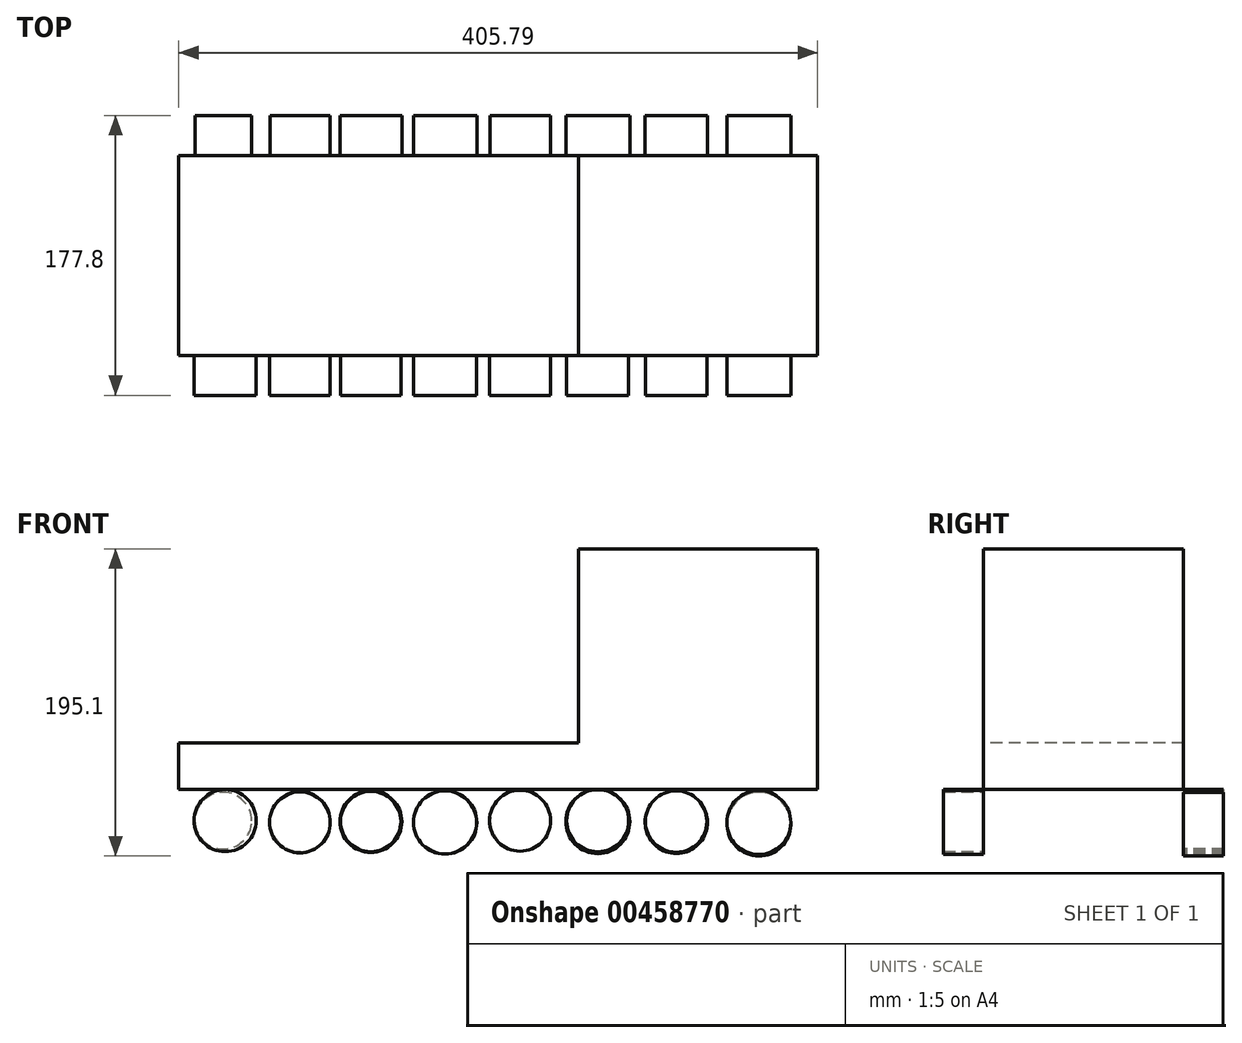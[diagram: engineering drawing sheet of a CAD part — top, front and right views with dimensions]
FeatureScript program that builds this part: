
annotation { "Feature Type Name" : "Feature", "Feature Type Description" : "" }
export const myFeature = defineFeature(function(context is Context, id is Id, definition is map)
    precondition{}
    {
        {
            var Q0;
            Q0=qCreatedBy(makeId("Front.planeOp"),FACE);
            var sketch = newSketch(context, id + "F0", { "sketchPlane" : qUnion([Q0])});
            skLineSegment(sketch, "E0.bottom", {"start": v(-76.2, 76.35) * mm, "end": v(75.6, 76.35) * mm});
            skLineSegment(sketch, "E0.top", {"start": v(-76.2, -76.35) * mm, "end": v(75.6, -76.35) * mm});
            skLineSegment(sketch, "E0.left", {"start": v(-76.2, 76.35) * mm, "end": v(-76.2, -76.35) * mm});
            skLineSegment(sketch, "E0.right", {"start": v(75.6, 76.35) * mm, "end": v(75.6, -76.35) * mm});
            skSolve(sketch);
        }
        {
            var Q0;
            Q0=makeQuery(id+"F0.imprint","IMPRINT",FACE,{"disambiguationData":[TD([[makeQuery(id+"F0.imprint","IMPRINT",EDGE,{"derivedFrom":sQuery(id+"F0.wireOp",EDGE,"E0.bottom")}),-1.0]])]});
            extrude(context, id + "F1", {"entities" : qUnion([Q0]), "depth" : 127 * mm});
        }
        {
            var Q0;
            Q0=makeQuery(id+"F1.opExtrude","SWEPT_FACE",FACE,{"disambiguationData":[OSD([sQuery(id+"F0.wireOp",EDGE,"E0.left")])]});
            var sketch = newSketch(context, id + "F2", { "sketchPlane" : qUnion([Q0])});
            skLineSegment(sketch, "E1.bottom", {"start": v(0, -46.8) * mm, "end": v(127, -46.8) * mm});
            skLineSegment(sketch, "E1.top", {"start": v(0, -76.35) * mm, "end": v(127, -76.35) * mm});
            skLineSegment(sketch, "E1.left", {"start": v(0, -46.8) * mm, "end": v(0, -76.35) * mm});
            skLineSegment(sketch, "E1.right", {"start": v(127, -46.8) * mm, "end": v(127, -76.35) * mm});
            skSolve(sketch);
        }
        {
            var Q0;
            Q0=makeQuery(id+"F2.imprint","IMPRINT",FACE,{"disambiguationData":[TD([[makeQuery(id+"F2.imprint","IMPRINT",EDGE,{"derivedFrom":sQuery(id+"F2.wireOp",EDGE,"E1.bottom")}),-1.0]])]});
            extrude(context, id + "F3", {"entities" : qUnion([Q0]), "operationType" : NewBodyOperationType.ADD, "depth" : 254 * mm});
        }
        {
            var Q0;
            Q0=makeQuery(id+"F3.boolean.opBoolean","MERGE",FACE,{"derivedFrom":[makeQuery(id+"F1.opExtrude","CAP_FACE",FACE,{"disambiguationData":[OSD([sQuery(id+"F0.wireOp",EDGE,"E0.bottom"),sQuery(id+"F0.wireOp",EDGE,"E0.top"),sQuery(id+"F0.wireOp",EDGE,"E0.left"),sQuery(id+"F0.wireOp",EDGE,"E0.right")])],"isStart":false}),makeQuery(id+"F3.opExtrude","SWEPT_FACE",FACE,{"disambiguationData":[OSD([sQuery(id+"F2.wireOp",EDGE,"E1.right")])]})]});
            var sketch = newSketch(context, id + "F4", { "sketchPlane" : qUnion([Q0])});
            skCircle(sketch, "E2", {"center": v(-300.7, -96.24) * mm, "radius": 19.7 * mm});
            skSolve(sketch);
        }
        {
            var Q0;
            Q0=makeQuery(id+"F4.imprint","IMPRINT",FACE,{"disambiguationData":[TD([[makeQuery(id+"F4.imprint","IMPRINT",EDGE,{"derivedFrom":makeQuery(id+"F1.opExtrude","CAP_EDGE",EDGE,{"disambiguationData":[OSD([sQuery(id+"F0.wireOp",EDGE,"E0.bottom")])],"isStart":false})}),-1.0]])]});
            var sketch = newSketch(context, id + "F5", { "sketchPlane" : qUnion([Q0])});
            skCircle(sketch, "E3", {"center": v(-253.23, -97.4) * mm, "radius": 19.32 * mm});
            skCircle(sketch, "E4", {"center": v(-208.22, -96.86) * mm, "radius": 19.15 * mm});
            skCircle(sketch, "E5", {"center": v(-161.07, -97.4) * mm, "radius": 20 * mm});
            skCircle(sketch, "E6", {"center": v(-113.38, -96.32) * mm, "radius": 19.36 * mm});
            skCircle(sketch, "E7", {"center": v(-64.09, -96.32) * mm, "radius": 19.7 * mm});
            skCircle(sketch, "E8", {"center": v(-14.26, -96.86) * mm, "radius": 19.5 * mm});
            skCircle(sketch, "E9", {"center": v(38.25, -97.4) * mm, "radius": 20.33 * mm});
            skSolve(sketch);
        }
        {
            var Q0;
            Q0=makeQuery(id+"F4.imprint","IMPRINT",FACE,{"disambiguationData":[TD([[makeQuery(id+"F4.imprint","IMPRINT",EDGE,{"derivedFrom":sQuery(id+"F4.wireOp",EDGE,"E2")}),1.0]])]});
            extrude(context, id + "F6", {"entities" : qUnion([Q0]), "depth" : 25.4 * mm});
        }
        {
            var Q0;
            Q0=makeQuery(id+"F5.imprint","IMPRINT",FACE,{"disambiguationData":[TD([[makeQuery(id+"F5.imprint","IMPRINT",EDGE,{"derivedFrom":sQuery(id+"F5.wireOp",EDGE,"E3")}),1.0]])]});
            var Q1;
            Q1=makeQuery(id+"F5.imprint","IMPRINT",FACE,{"disambiguationData":[TD([[makeQuery(id+"F5.imprint","IMPRINT",EDGE,{"derivedFrom":sQuery(id+"F5.wireOp",EDGE,"E4")}),1.0]])]});
            var Q2;
            Q2=makeQuery(id+"F5.imprint","IMPRINT",FACE,{"disambiguationData":[TD([[makeQuery(id+"F5.imprint","IMPRINT",EDGE,{"derivedFrom":sQuery(id+"F5.wireOp",EDGE,"E5")}),1.0]])]});
            var Q3;
            Q3=makeQuery(id+"F5.imprint","IMPRINT",FACE,{"disambiguationData":[TD([[makeQuery(id+"F5.imprint","IMPRINT",EDGE,{"derivedFrom":sQuery(id+"F5.wireOp",EDGE,"E6")}),1.0]])]});
            var Q4;
            Q4=makeQuery(id+"F5.imprint","IMPRINT",FACE,{"disambiguationData":[TD([[makeQuery(id+"F5.imprint","IMPRINT",EDGE,{"derivedFrom":sQuery(id+"F5.wireOp",EDGE,"E7")}),1.0]])]});
            var Q5;
            Q5=makeQuery(id+"F5.imprint","IMPRINT",FACE,{"disambiguationData":[TD([[makeQuery(id+"F5.imprint","IMPRINT",EDGE,{"derivedFrom":sQuery(id+"F5.wireOp",EDGE,"E8")}),1.0]])]});
            var Q6;
            Q6=makeQuery(id+"F5.imprint","IMPRINT",FACE,{"disambiguationData":[TD([[makeQuery(id+"F5.imprint","IMPRINT",EDGE,{"derivedFrom":sQuery(id+"F5.wireOp",EDGE,"E9")}),1.0]])]});
            extrude(context, id + "F7", {"entities" : qUnion([Q0, Q1, Q2, Q3, Q4, Q5, Q6]), "depth" : 25.4 * mm});
        }
        {
            var Q0;
            Q0=makeQuery(id+"F3.boolean.opBoolean","MERGE",FACE,{"derivedFrom":[makeQuery(id+"F1.opExtrude","CAP_FACE",FACE,{"disambiguationData":[OSD([sQuery(id+"F0.wireOp",EDGE,"E0.bottom"),sQuery(id+"F0.wireOp",EDGE,"E0.top"),sQuery(id+"F0.wireOp",EDGE,"E0.left"),sQuery(id+"F0.wireOp",EDGE,"E0.right")])],"isStart":true}),makeQuery(id+"F3.opExtrude","SWEPT_FACE",FACE,{"disambiguationData":[OSD([sQuery(id+"F2.wireOp",EDGE,"E1.left")])]})]});
            var sketch = newSketch(context, id + "F8", { "sketchPlane" : qUnion([Q0])});
            skCircle(sketch, "E10", {"center": v(-38.35, -98.47) * mm, "radius": 20.28 * mm});
            skCircle(sketch, "E11", {"center": v(14.16, -97.4) * mm, "radius": 19.77 * mm});
            skCircle(sketch, "E12", {"center": v(64, -96.86) * mm, "radius": 20.37 * mm});
            skCircle(sketch, "E13", {"center": v(113.29, -96.32) * mm, "radius": 19.08 * mm});
            skCircle(sketch, "E14", {"center": v(160.98, -97.4) * mm, "radius": 20.11 * mm});
            skCircle(sketch, "E15", {"center": v(208.13, -96.86) * mm, "radius": 19.62 * mm});
            skCircle(sketch, "E16", {"center": v(253.14, -96.86) * mm, "radius": 19.08 * mm});
            skCircle(sketch, "E17", {"center": v(301.9, -96.32) * mm, "radius": 18.01 * mm});
            skSolve(sketch);
        }
        {
            var Q0;
            Q0=makeQuery(id+"F8.imprint","IMPRINT",FACE,{"disambiguationData":[TD([[makeQuery(id+"F8.imprint","IMPRINT",EDGE,{"derivedFrom":sQuery(id+"F8.wireOp",EDGE,"E10")}),1.0]])]});
            var Q1;
            Q1=makeQuery(id+"F8.imprint","IMPRINT",FACE,{"disambiguationData":[TD([[makeQuery(id+"F8.imprint","IMPRINT",EDGE,{"derivedFrom":sQuery(id+"F8.wireOp",EDGE,"E11")}),1.0]])]});
            var Q2;
            Q2=makeQuery(id+"F8.imprint","IMPRINT",FACE,{"disambiguationData":[TD([[makeQuery(id+"F8.imprint","IMPRINT",EDGE,{"derivedFrom":sQuery(id+"F8.wireOp",EDGE,"E12")}),1.0]])]});
            var Q3;
            Q3=makeQuery(id+"F8.imprint","IMPRINT",FACE,{"disambiguationData":[TD([[makeQuery(id+"F8.imprint","IMPRINT",EDGE,{"derivedFrom":sQuery(id+"F8.wireOp",EDGE,"E13")}),1.0]])]});
            var Q4;
            Q4=makeQuery(id+"F8.imprint","IMPRINT",FACE,{"disambiguationData":[TD([[makeQuery(id+"F8.imprint","IMPRINT",EDGE,{"derivedFrom":sQuery(id+"F8.wireOp",EDGE,"E14")}),1.0]])]});
            var Q5;
            Q5=makeQuery(id+"F8.imprint","IMPRINT",FACE,{"disambiguationData":[TD([[makeQuery(id+"F8.imprint","IMPRINT",EDGE,{"derivedFrom":sQuery(id+"F8.wireOp",EDGE,"E15")}),1.0]])]});
            var Q6;
            Q6=makeQuery(id+"F8.imprint","IMPRINT",FACE,{"disambiguationData":[TD([[makeQuery(id+"F8.imprint","IMPRINT",EDGE,{"derivedFrom":sQuery(id+"F8.wireOp",EDGE,"E16")}),1.0]])]});
            var Q7;
            Q7=makeQuery(id+"F8.imprint","IMPRINT",FACE,{"disambiguationData":[TD([[makeQuery(id+"F8.imprint","IMPRINT",EDGE,{"derivedFrom":sQuery(id+"F8.wireOp",EDGE,"E17")}),1.0]])]});
            extrude(context, id + "F9", {"entities" : qUnion([Q0, Q1, Q2, Q3, Q4, Q5, Q6, Q7]), "depth" : 25.4 * mm});
        }
    });
